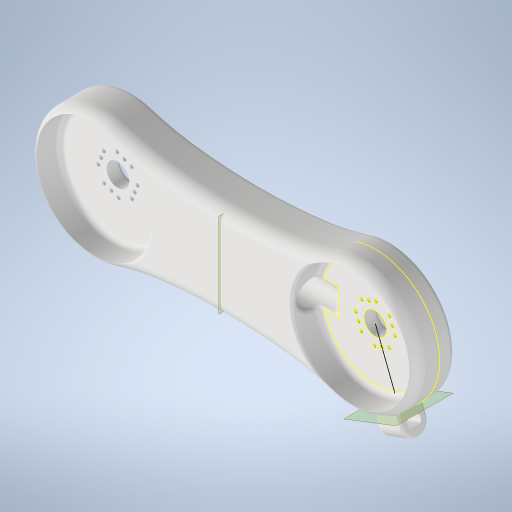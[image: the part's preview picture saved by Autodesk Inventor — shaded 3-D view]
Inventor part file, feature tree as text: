
AUTODESK INVENTOR PART (.ipt)
format: ipt  version: 2024 (Build 280153000, 153)  size: 1,647,104 bytes
history: native  units: mm
features: fillet x15, extrude x9, other x4, plane x3, projected_geometry x3, mirror x2, reference x1, sketch x1
ambient origin geometry x8: Origin, YZ Plane, XZ Plane, XY Plane, X Axis, Y Axis, Z Axis, Center Point
bodies: Solid1 (feature_tree)
feature tree (38):
  plane  "Work Plane1"
  extrude  "Extrusion1"  Depth=1.0mm TaperAngle=0.0deg
  extrude  "Extrusion2"  Depth=1.0mm
  extrude  "Extrusion3"  Depth=1.0mm TaperAngle=0.0deg
  extrude  "Extrusion4"  Depth=1.0mm
  extrude  "Extrusion5"  Depth=1.0mm
  fillet  "Fillet1"  Radius=15.0mm
  fillet  "Fillet2"  Radius=10.0mm
  fillet  "Fillet3"  Radius=20.0mm
  plane  "Work Plane3"
  mirror  "Mirror2"
  mirror  "Mirror3"
  fillet  "Fillet4"  Radius=20.0mm
  fillet  "Fillet5"  Radius=2.837941mm
  extrude  "Extrusion6"  Depth=1.0mm
  fillet  "Fillet6"  Radius=6.0mm
  fillet  "Fillet7"  Radius=10.0mm
  fillet  "Fillet10"  Radius=8.0mm
  fillet  "Fillet11"  Radius=10.0mm
  fillet  "Fillet12"  Radius=2.0mm
  fillet  "Fillet13"  Radius=2.0mm
  plane  "Work Plane5"
  extrude  "Extrusion11"  Depth=1.0mm
  extrude  "Extrusion12"  TaperAngle=0.0deg  [1 undecoded]
  extrude  "Extrusion13"  Depth=1.0mm
  fillet  "Fillet14"  Radius=100.0mm
  fillet  "Fillet15"  Radius=70.0mm
  fillet  "Fillet16"  Radius=1.0mm
  fillet  "Fillet17"  Radius=1.0mm
  reference  "Reference1"
  projected_geometry  "Projected Loop1"
  sketch  "Sketch3"  dims[d0=50.0mm d1=6.0mm d2=0.0mm d3=45.0mm d4=10.0mm d5=0.0mm d6=50.0mm d7=15.0mm d8=15.0mm d9=10.0mm d10=0.0mm d12=20.0mm d13=20.0mm d14=2.837941mm d15=12.817996mm d16=6.0mm d17=0.0mm d18=10.0mm d19=8.0mm d20=10.0mm d21=0.0mm d22=2.0mm d23=2.0mm d24=1.0mm d25=0.0mm d26=200.0mm d27=100.0mm d28=70.0mm d29=0.0mm d30=1.0mm d31=1.0mm d53=5.0mm d54=2.0mm d55=2.0mm d56=2.0mm d57=10.0mm d58=10.0mm d59=2.5mm d60=0.0mm d61=9.0mm d62=0.0mm d63=5.0mm d64=3.0mm d65=5.0mm d66=5.0mm d67=0.0mm d68=0.0mm d69=1.0mm d70=1.0mm d71=5.0mm d72=1.0mm]
  projected_geometry  "Projected Loop2"
  projected_geometry  "Projected Loop3"
  other  "<userpath> windows\Documents\Inventor\Robotska_roka\Assembly4.iam"
  other  "Assembly4.iam"
  other  "Servo Motor MG996R  With Attachments:4"
  other  "attachmentCircular_1"
note: 1 required parameter value undecoded (feature->parameter linkage not recoverable at this tier; creation-order binding heuristic only, values carry confidence <= 0.55)
